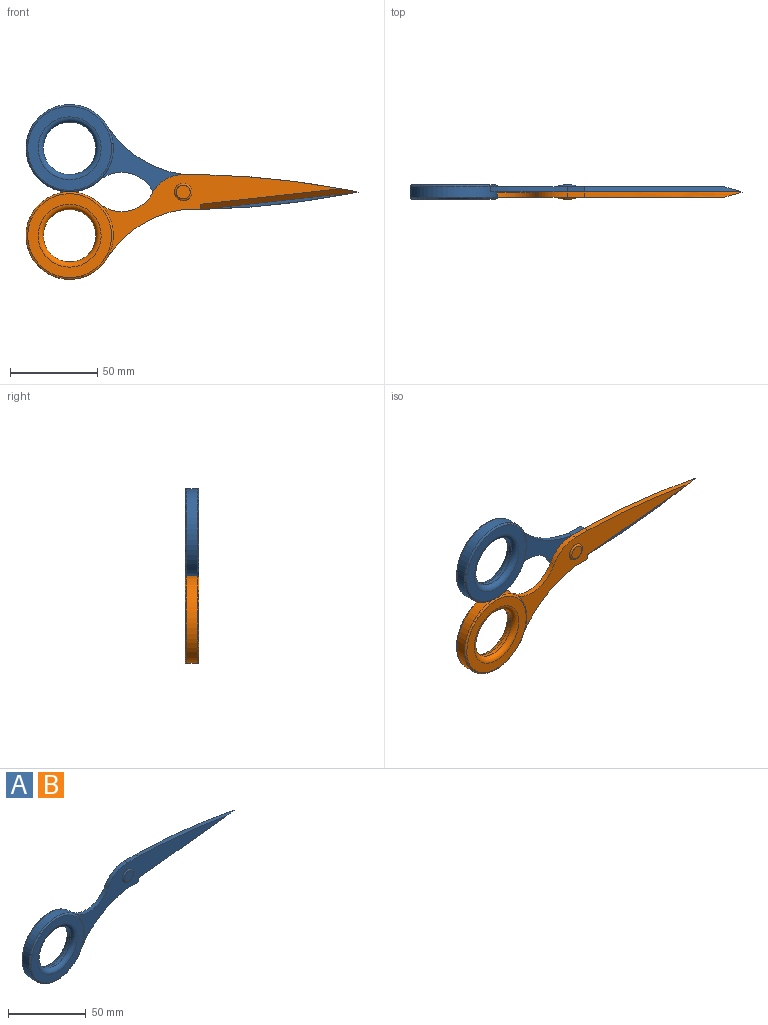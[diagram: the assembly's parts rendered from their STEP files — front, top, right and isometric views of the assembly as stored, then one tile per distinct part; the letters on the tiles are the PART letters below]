
ASSEMBLY  parts=2 mates=1
PART A: 20 faces, bbox 192.1x8x62.1 mm
  f0: plane 138.65x48.36mm, normal (0,-1,0), area 1570.1mm2, adj f2,f3,f4,f5,f7,f8,f13,f14
  f1: plane 148.49x48.36mm, normal (0,1,0), area 1904mm2, adj f2,f3,f4,f5,f6,f7,f8,f13
  f2: plane 10x3mm, normal (0,0,1), area 30mm2, adj f0,f1,f4,f8
  f3: plane 10x3mm, normal (0,0,-1), area 30mm2, adj f0,f1,f7,f14
  f4: cylinder r=500mm len=90mm, axis (0,1,0), area 257.2mm2, adj f0,f1,f2,f13
  f5: cylinder r=20mm len=31.17mm, axis (0,1,0), area 110.2mm2, adj f0,f1,f6,f8
  f6: cylinder r=25mm len=50mm, axis (0,1,0), area 836.5mm2, adj f1,f5,f7,f17,f18
  f7: cylinder r=62.19mm len=43.87mm, axis (0,1,0), area 161.7mm2, adj f0,f1,f3,f6
  f8: cylinder r=20mm len=17.32mm, axis (0,1,0), area 62.8mm2, adj f0,f1,f2,f5
  f9: plane 48x48mm, normal (0,1,0), area 791.7mm2, adj f15,f17
  f10: cylinder r=15mm len=30mm, axis (0,1,0), area 188.5mm2, adj f15,f16
  f11: plane 48x48mm, normal (0,-1,0), area 791.7mm2, adj f16,f18
  f12: plane 8x8mm, normal (0,-1,0), area 50.3mm2, adj f19
  f13: plane 90x11.91mm, normal (0.08,-0.7,-0.7), area 362.3mm2, adj f0,f1,f4,f14
  f14: plane 3x3mm, normal (1,0,0), area 4.5mm2, adj f0,f3,f13
  f15: torus R=18mm, axis (0,-1,0), area 476.4mm2, adj f9,f10
  f16: torus R=18mm, axis (0,-1,0), area 476.4mm2, adj f10,f11
  f17: torus R=24mm, axis (0,-1,0), area 243.2mm2, adj f6,f9
  f18: torus R=24mm, axis (0,-1,0), area 243.2mm2, adj f0,f6,f11
  f19: torus R=4mm, axis (0,-1,0), area 45.8mm2, adj f0,f12
PART B: same geometry as A
PLACE A rot(axis=(1,0,0),180deg) t=(11.92,-6.33,-19.82)mm
PLACE B t=(11.92,-6.33,-19.82)mm fixed
MATE revolute B.f19 <-> A.f19  axis (0,-1,0) through (11.92,-6.33,-19.82)mm
